# Revit family: Aquatica_Downtown_Spa_with_Maridur_white
name_source: partatom
category: Plumbing Fixtures
revit_build: Autodesk Revit 2018 (Build: 20190510_1515(x64)
units: mm (PartAtom-declared; Revit-internal decimal feet)

## family parameters
Always vertical = Yes
Cut with Voids When Loaded = No
OmniClass Number = 23.45.00.00
OmniClass Title = Sanitary, Laundry, and Cleaning Equipment
Part Type = Normal
Room Calculation Point = No
Round Connector Dimension = Use Diameter
Shared = No
Work Plane-Based = No

## types (1)
- Color - (White) Size - (200,5x150,5x80,5 cm)
    Assembly required = No
    Audio Material = Aquatica-Gray
    Circuits required = 1 Single Circuit
    Country where manufactured = EU
    Current = 32 A
    Depth to overflow drain (cm) = 52
    Description = Aquatica presents our all-new, genuinely designed Downtown hot tub, the most beautiful, minimalist hydro-massage spa in the market! Ideal for couples, it will find a place in suites or superior hotel rooms but also in private homes. The Downtown model is the perfect choice for anyone interested in buying a top-of-the-line, high-performance spa for romance, family enjoyment, partying, or socializing with friends.
    Display Material = Aquatica-Black
    Drain placement = Reversible
    Electrical standards = 220-240V/50/60Hz
    Exterior dimensions (cm) = 200,5 L x 150,5 W x 80,5 H
    Frequency = 50-60 Hz
    Installation type = Freestanding
    Interior dimensions (cm) = 167,5 L x 115,7 W x 60 H
    Load Classification = Power
    Manufacturer = Aquatica
    Metal Material = Aquatica-Metal-Silver
    Model = Downtown
    Number of boxes = 1
    Package dimensions (cm) = 220 L x 170 W x 116.5 H
    Product Material = Aquatica-White-High-Gloss
    Product color = White
    Product material = DurateX™ Tub Shell With Maridur® Siding
    Product weight = 249 kg
    SKU = Downtown-Spa-Maridur
    Shape = Rectangular
    Shipping weight (kg) = 448,2
    Surface finish = High Gloss
    URL = https://www.aquaticabath.eu
    Voltage = 220 V
    Warranty = 10 Year Limited Warranty on the bathtub shell
    Water capacity = 735 liters

## geometry (parser evidence)
native form markers: Sweep x5
no freeform markers — native parametric forms only
